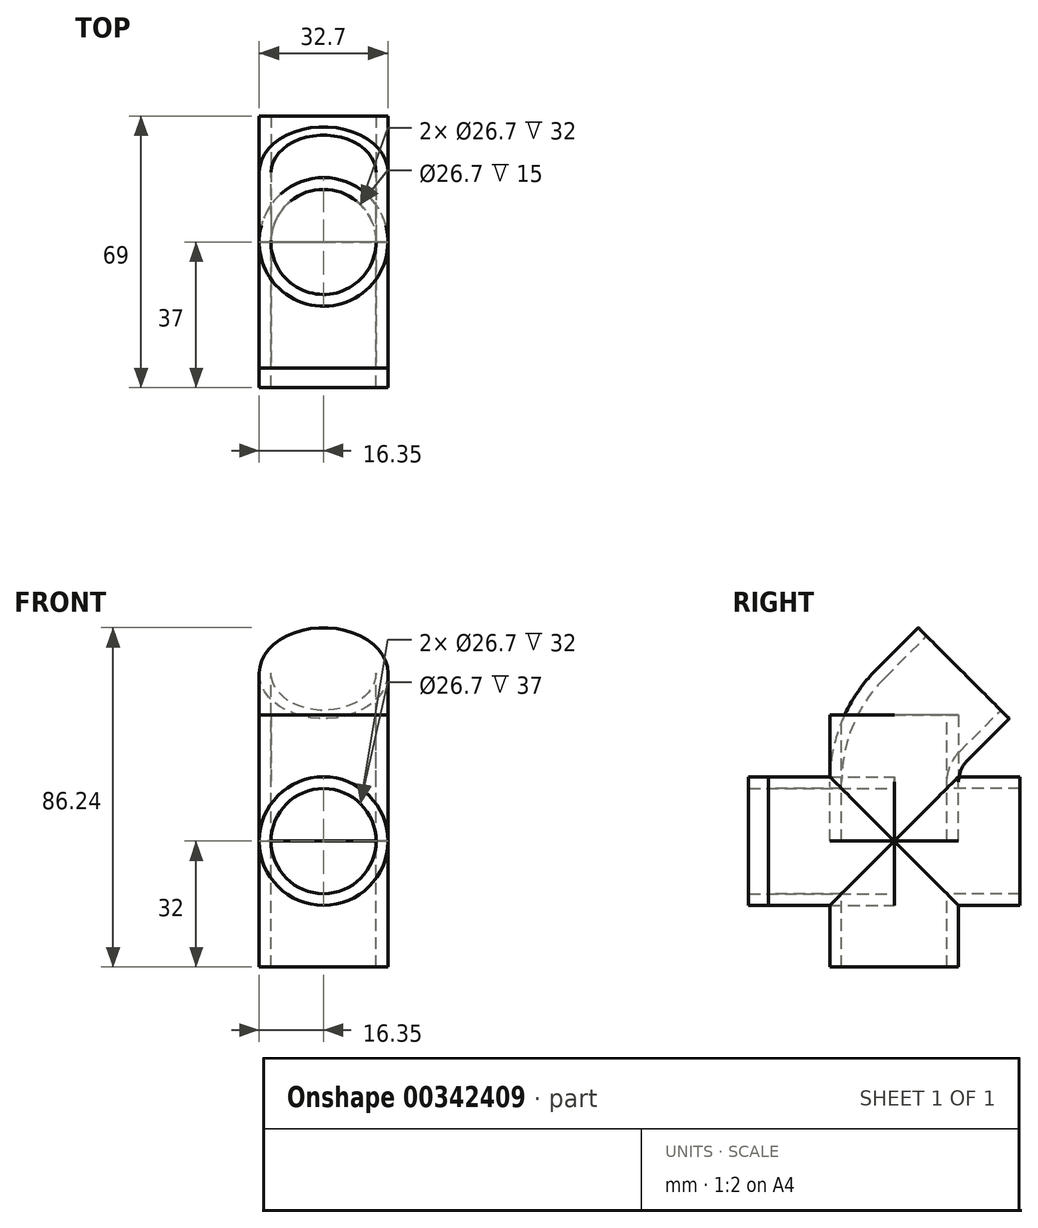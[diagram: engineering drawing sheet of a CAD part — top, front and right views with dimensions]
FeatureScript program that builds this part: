
annotation { "Feature Type Name" : "Feature", "Feature Type Description" : "" }
export const myFeature = defineFeature(function(context is Context, id is Id, definition is map)
    precondition{}
    {
        {
            var Q0;
            Q0=qCreatedBy(makeId("Front.planeOp"),FACE);
            var sketch = newSketch(context, id + "F0", { "sketchPlane" : qUnion([Q0])});
            skCircle(sketch, "E0", {"center": v(0, 0) * mm, "radius": 16.35 * mm});
            skCircle(sketch, "E1", {"center": v(0, 0) * mm, "radius": 13.35 * mm});
            skSolve(sketch);
        }
        {
            var Q0;
            Q0=makeQuery(id+"F0.imprint","IMPRINT",FACE,{"disambiguationData":[TD([[makeQuery(id+"F0.imprint","IMPRINT",EDGE,{"derivedFrom":sQuery(id+"F0.wireOp",EDGE,"E1")}),1.0]])]});
            var Q1;
            Q1=makeQuery(id+"F0.imprint","IMPRINT",FACE,{"disambiguationData":[TD([[makeQuery(id+"F0.imprint","IMPRINT",EDGE,{"derivedFrom":sQuery(id+"F0.wireOp",EDGE,"E0")}),1.0]])]});
            extrude(context, id + "F1", {"entities" : qUnion([Q0, Q1]), "endBound" : BoundingType.SYMMETRIC, "depth" : 64 * mm});
        }
        {
            var Q0;
            Q0=qCreatedBy(makeId("Top.planeOp"),FACE);
            var sketch = newSketch(context, id + "F2", { "sketchPlane" : qUnion([Q0])});
            skCircle(sketch, "E2", {"center": v(0, 0) * mm, "radius": 16.35 * mm});
            skCircle(sketch, "E3", {"center": v(0, 0) * mm, "radius": 13.35 * mm});
            skSolve(sketch);
        }
        {
            var Q0;
            Q0=makeQuery(id+"F2.imprint","IMPRINT",FACE,{"disambiguationData":[TD([[makeQuery(id+"F2.imprint","IMPRINT",EDGE,{"derivedFrom":sQuery(id+"F2.wireOp",EDGE,"E2")}),1.0]])]});
            var Q1;
            Q1=makeQuery(id+"F2.imprint","IMPRINT",FACE,{"disambiguationData":[TD([[makeQuery(id+"F2.imprint","IMPRINT",EDGE,{"derivedFrom":sQuery(id+"F2.wireOp",EDGE,"E3")}),1.0]])]});
            extrude(context, id + "F3", {"entities" : qUnion([Q0, Q1]), "operationType" : NewBodyOperationType.ADD, "depth" : 32 * mm});
        }
        {
            var Q0;
            Q0=makeQuery(id+"F0.imprint","IMPRINT",FACE,{"disambiguationData":[TD([[makeQuery(id+"F0.imprint","IMPRINT",EDGE,{"derivedFrom":sQuery(id+"F0.wireOp",EDGE,"E1")}),1.0]])]});
            var Q1;
            Q1=sQuery(id+"F0.wireOp",EDGE,"E1");
            extrude(context, id + "F4", {"entities" : qUnion([Q0]), "operationType" : NewBodyOperationType.REMOVE, "surfaceEntities" : qUnion([Q1]), "endBound" : BoundingType.SYMMETRIC, "oppositeDirection" : true, "depth" : 74 * mm});
        }
        {
            var Q0;
            Q0=makeQuery(id+"F2.imprint","IMPRINT",FACE,{"disambiguationData":[TD([[makeQuery(id+"F2.imprint","IMPRINT",EDGE,{"derivedFrom":sQuery(id+"F2.wireOp",EDGE,"E3")}),1.0]])]});
            extrude(context, id + "F5", {"entities" : qUnion([Q0]), "operationType" : NewBodyOperationType.REMOVE, "endBound" : BoundingType.THROUGH_ALL, "depth" : 25 * mm});
        }
        {
            var Q0;
            Q0=makeQuery(id+"F0.imprint","IMPRINT",FACE,{"disambiguationData":[TD([[makeQuery(id+"F0.imprint","IMPRINT",EDGE,{"derivedFrom":sQuery(id+"F0.wireOp",EDGE,"E1")}),1.0]])]});
            var Q1;
            Q1=makeQuery(id+"F0.imprint","IMPRINT",FACE,{"disambiguationData":[TD([[makeQuery(id+"F0.imprint","IMPRINT",EDGE,{"derivedFrom":sQuery(id+"F0.wireOp",EDGE,"E0")}),1.0]])]});
            extrude(context, id + "F6", {"entities" : qUnion([Q0, Q1]), "endBound" : BoundingType.SYMMETRIC, "depth" : 64 * mm});
        }
        {
            var Q0;
            Q0=makeQuery(id+"F2.imprint","IMPRINT",FACE,{"disambiguationData":[TD([[makeQuery(id+"F2.imprint","IMPRINT",EDGE,{"derivedFrom":sQuery(id+"F2.wireOp",EDGE,"E3")}),1.0]])]});
            var Q1;
            Q1=makeQuery(id+"F2.imprint","IMPRINT",FACE,{"disambiguationData":[TD([[makeQuery(id+"F2.imprint","IMPRINT",EDGE,{"derivedFrom":sQuery(id+"F2.wireOp",EDGE,"E2")}),1.0]])]});
            extrude(context, id + "F7", {"entities" : qUnion([Q0, Q1]), "operationType" : NewBodyOperationType.ADD, "endBound" : BoundingType.SYMMETRIC, "depth" : 64 * mm});
        }
        {
            var Q0;
            Q0=makeQuery(id+"F0.imprint","IMPRINT",FACE,{"disambiguationData":[TD([[makeQuery(id+"F0.imprint","IMPRINT",EDGE,{"derivedFrom":sQuery(id+"F0.wireOp",EDGE,"E1")}),1.0]])]});
            extrude(context, id + "F8", {"entities" : qUnion([Q0]), "operationType" : NewBodyOperationType.REMOVE, "endBound" : BoundingType.SYMMETRIC, "oppositeDirection" : true, "depth" : 64 * mm});
        }
        {
            var Q0;
            Q0=makeQuery(id+"F2.imprint","IMPRINT",FACE,{"disambiguationData":[TD([[makeQuery(id+"F2.imprint","IMPRINT",EDGE,{"derivedFrom":sQuery(id+"F2.wireOp",EDGE,"E3")}),1.0]])]});
            extrude(context, id + "F9", {"entities" : qUnion([Q0]), "operationType" : NewBodyOperationType.REMOVE, "endBound" : BoundingType.SYMMETRIC, "oppositeDirection" : true, "depth" : 64 * mm});
        }
        {
            var Q0;
            Q0=makeQuery(id+"F0.imprint","IMPRINT",FACE,{"disambiguationData":[TD([[makeQuery(id+"F0.imprint","IMPRINT",EDGE,{"derivedFrom":sQuery(id+"F0.wireOp",EDGE,"E0")}),1.0]])]});
            extrude(context, id + "F10", {"entities" : qUnion([Q0]), "depth" : 37 * mm});
        }
        {
            var Q0;
            Q0=qCreatedBy(makeId("Right.planeOp"),FACE);
            var sketch = newSketch(context, id + "F11", { "sketchPlane" : qUnion([Q0])});
            skLineSegment(sketch, "E4", {"start": v(0, 0) * mm, "end": v(0, 15) * mm});
            skLineSegment(sketch, "E5", {"start": v(7.07, 32.07) * mm, "end": v(17.68, 42.68) * mm});
            skArc(sketch, "E6", {"start": v(7.07, 32.07) * mm, "mid": v(1.84, 24.24) * mm, "end": v(0, 15) * mm});
            skLineSegment(sketch, "E7", {"start": v(7.07, 32.07) * mm, "end": v(0, 25) * mm, "construction": true});
            skLineSegment(sketch, "E8", {"start": v(0, 15) * mm, "end": v(0, 25) * mm, "construction": true});
            skSolve(sketch);
        }
        {
            var Q0;
            Q0=makeQuery(id+"F2.imprint","IMPRINT",FACE,{"disambiguationData":[TD([[makeQuery(id+"F2.imprint","IMPRINT",EDGE,{"derivedFrom":sQuery(id+"F2.wireOp",EDGE,"E2")}),1.0]])]});
            var Q1;
            Q1 = qConstructionFilter(qBodyType(qCreatedBy(id + "F11" ,EDGE), BodyType.WIRE), ConstructionObject.NO);
            sweep(context, id + "F12", {"profiles" : qUnion([Q0]), "path" : qUnion([Q1])});
        }
    });
